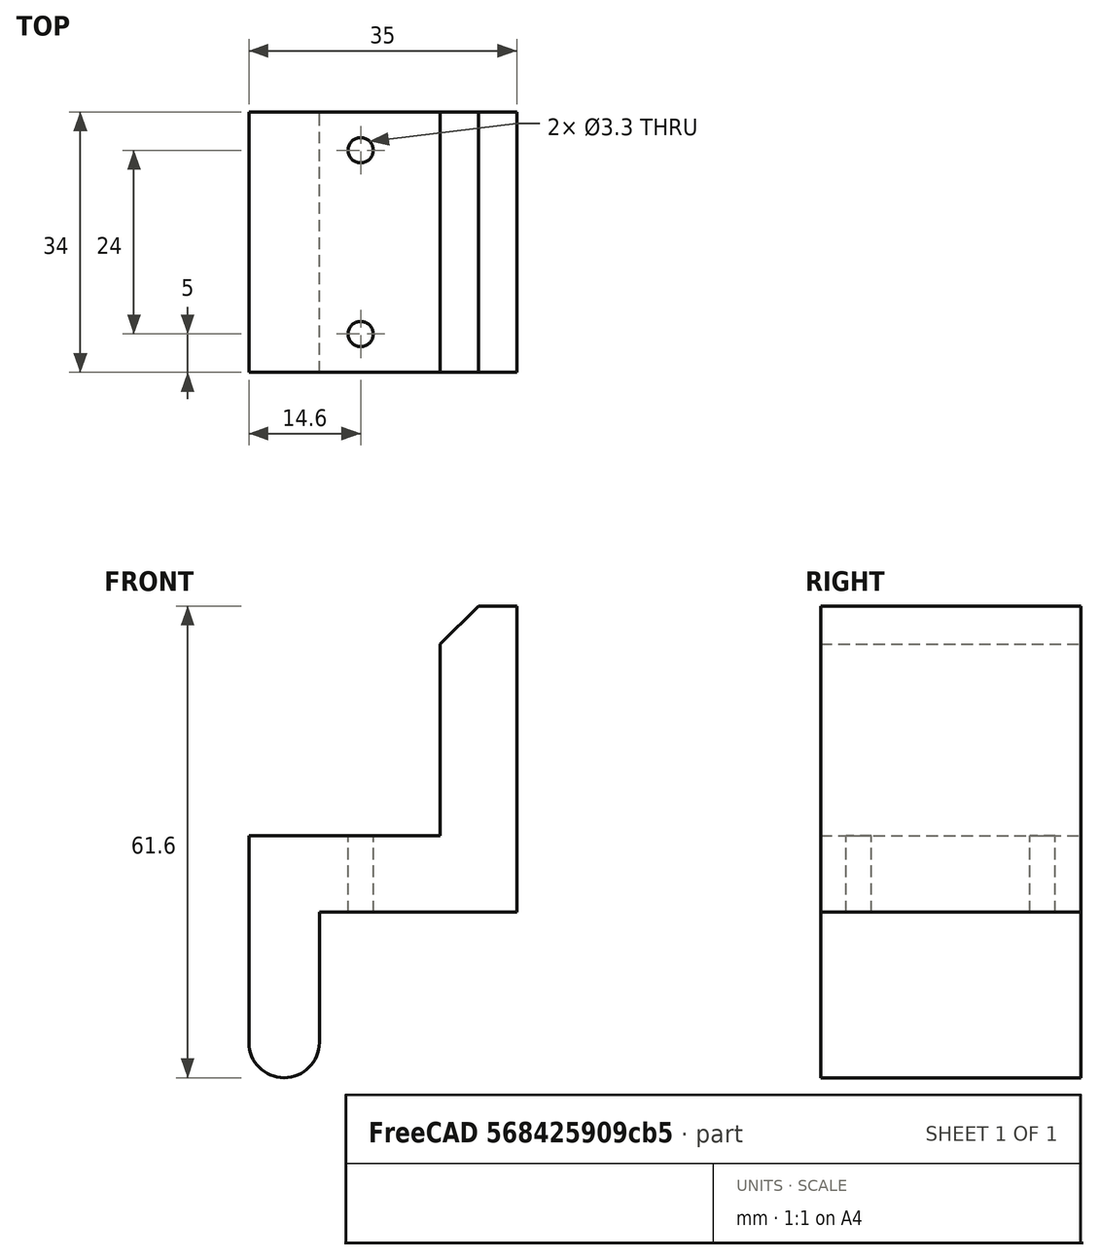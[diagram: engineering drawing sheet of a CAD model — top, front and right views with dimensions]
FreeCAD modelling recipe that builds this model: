
FCSTD DOCUMENT  (FreeCAD 0.15R4671 (Git))
Label: edge_mount_bottom
License: All rights reserved
LicenseURL: http://en.wikipedia.org/wiki/All_rights_reserved
objects: Part::Cylinder×3, Part::Box×3, Part::MultiFuse×3, Part::Cut×1, Part::Chamfer×1
note: 11 computed .brp shape members not serialized (recipe doc carries the construction recipe); baked Part::Feature solids carry a one-line shape summary decoded from their .brp

FEATURE [Part::Cylinder] Cylinder
  Angle = 360
  Height = 34
  Placement = pos=(0,0,0) rot=(-1,0,0;1.5708rad)
  Radius = 4.6
FEATURE [Part::Box] Box  label="Cube"
  Height = 17
  Length = 9.2
  Placement = pos=(-4.6,0,0) rot=(0,0,1;0rad)
  Width = 34
FEATURE [Part::Box] Box001  label="Cube001"
  Height = 10
  Length = 35
  Placement = pos=(-4.6,0,17) rot=(0,0,1;0rad)
  Width = 34
FEATURE [Part::Cylinder] Cylinder001
  Angle = 360
  Height = 20
  Placement = pos=(10,5,7) rot=(0,0,1;0rad)
  Radius = 1.65
FEATURE [Part::Cylinder] Cylinder002
  Angle = 360
  Height = 20
  Placement = pos=(10,29,7) rot=(0,0,1;0rad)
  Radius = 1.65
FEATURE [Part::MultiFuse] Fusion001
  Shapes = -> [Cylinder002,Cylinder001]
FEATURE [Part::MultiFuse] Fusion
  Shapes = -> [Cylinder,Box001,Box]
FEATURE [Part::Cut] Cut
  Base = -> Fusion
  Tool = -> Fusion001
FEATURE [Part::Box] Box002  label="Cube002"
  Height = 30
  Length = 10
  Placement = pos=(20.4,0,27) rot=(0,0,1;0rad)
  Width = 34
FEATURE [Part::Chamfer] Chamfer
  Base = -> Box002
  Edges = 1 edges r=5: [Edge2]
FEATURE [Part::MultiFuse] Fusion002
  Shapes = -> [Cut,Chamfer]
